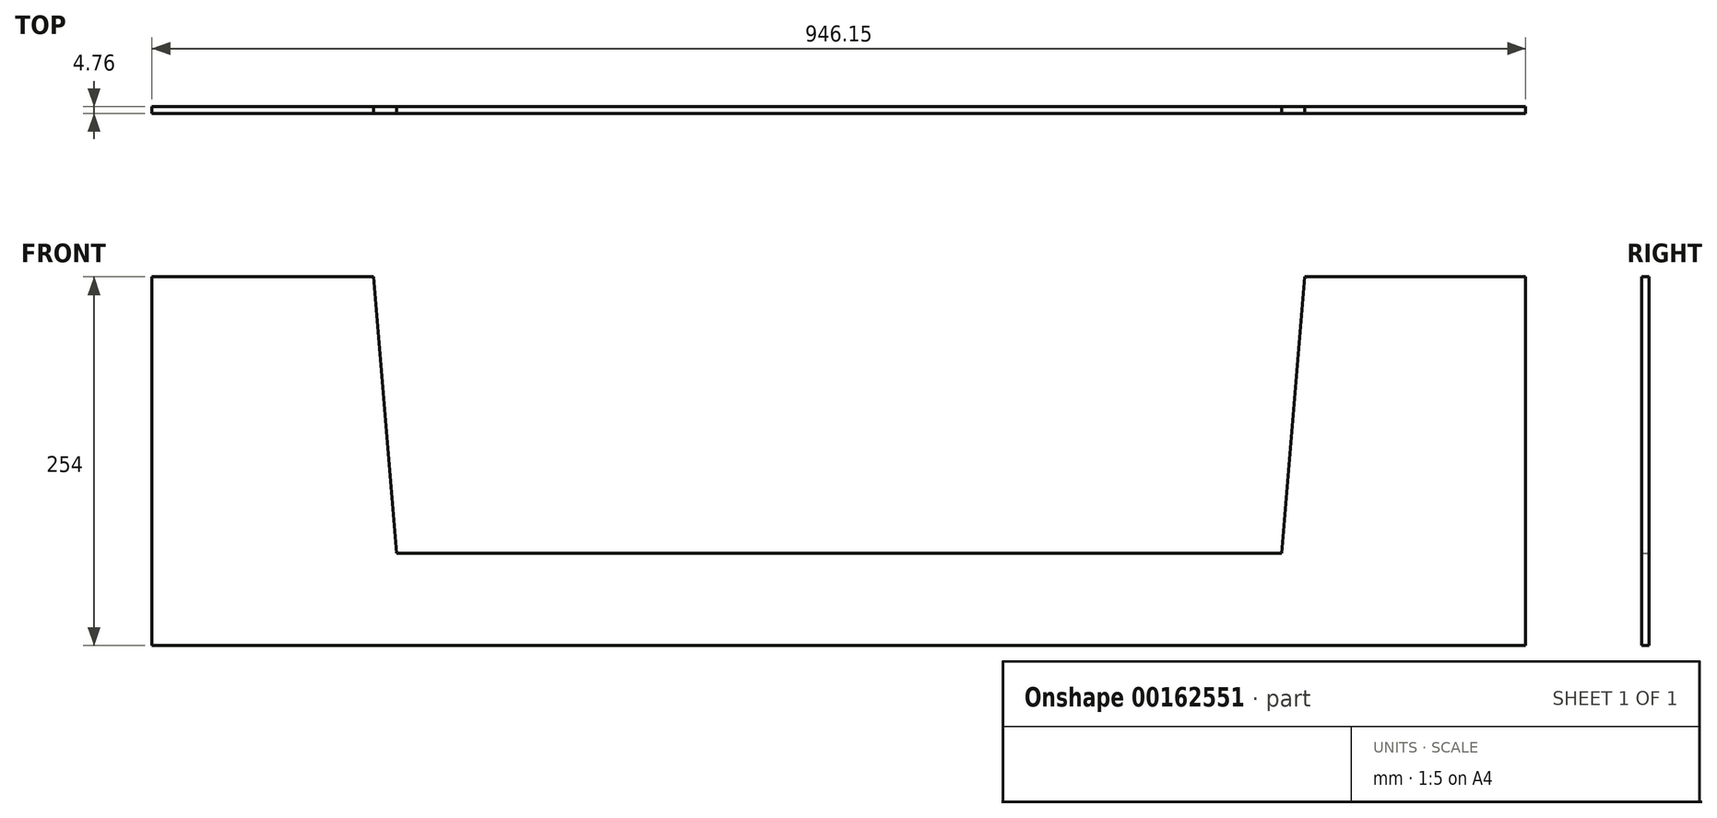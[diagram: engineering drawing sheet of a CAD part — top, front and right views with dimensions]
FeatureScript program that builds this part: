
annotation { "Feature Type Name" : "Feature", "Feature Type Description" : "" }
export const myFeature = defineFeature(function(context is Context, id is Id, definition is map)
    precondition{}
    {
        {
            var Q0;
            Q0=qCreatedBy(makeId("Front.planeOp"),FACE);
            var sketch = newSketch(context, id + "F0", { "sketchPlane" : qUnion([Q0])});
            skLineSegment(sketch, "E0.top", {"start": v(486.51, -127) * mm, "end": v(-459.64, -127) * mm});
            skLineSegment(sketch, "E0.left", {"start": v(486.51, 127) * mm, "end": v(486.51, -127) * mm});
            skLineSegment(sketch, "E0.right", {"start": v(-459.64, 127) * mm, "end": v(-459.64, -127) * mm});
            skPoint(sketch, "E0.middle", {"position": v(13.44, 0) * mm});
            skLineSegment(sketch, "E1.top", {"start": v(-291.36, -63.5) * mm, "end": v(318.24, -63.5) * mm});
            skLineSegment(sketch, "E2.trimOffspring", {"start": v(-307.24, 127) * mm, "end": v(-459.64, 127) * mm});
            skLineSegment(sketch, "E3", {"start": v(486.51, 127) * mm, "end": v(334.11, 127) * mm});
            skLineSegment(sketch, "E4", {"start": v(-291.36, -63.5) * mm, "end": v(-307.24, 127) * mm});
            skLineSegment(sketch, "E5", {"start": v(318.24, -63.5) * mm, "end": v(334.11, 127) * mm});
            skPoint(sketch, "E6.orphan", {"position": v(-367.8, 127) * mm});
            skPoint(sketch, "E1.right.start.orphan", {"position": v(394.44, 127) * mm});
            skSolve(sketch);
        }
        {
            var Q0;
            Q0=qSketchRegion(id+"F0",true);
            extrude(context, id + "F1", {"entities" : qUnion([Q0]), "depth" : 4.76 * mm});
        }
    });
